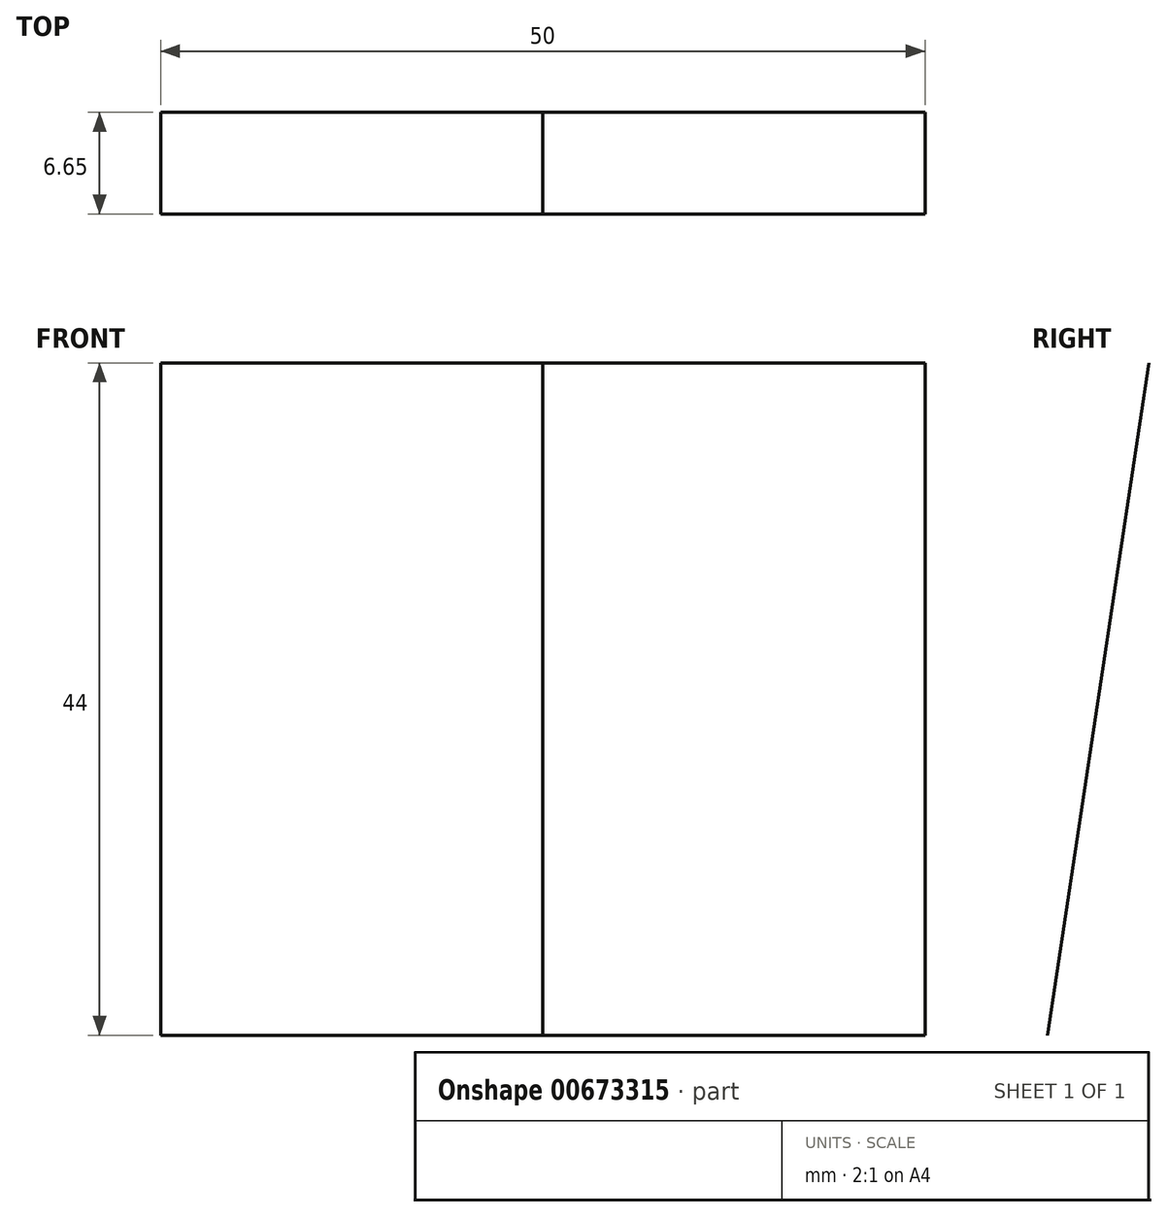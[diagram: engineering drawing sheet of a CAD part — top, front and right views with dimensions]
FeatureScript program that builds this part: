
annotation { "Feature Type Name" : "Feature", "Feature Type Description" : "" }
export const myFeature = defineFeature(function(context is Context, id is Id, definition is map)
    precondition{}
    {
        {
            var Q0;
            Q0=qCreatedBy(makeId("Right.planeOp"),FACE);
            var sketch = newSketch(context, id + "F0", { "sketchPlane" : qUnion([Q0])});
            skLineSegment(sketch, "E0", {"start": v(33.53, 0) * mm, "end": v(27.42, 43.92) * mm});
            skLineSegment(sketch, "E1", {"start": v(14.85, 44) * mm, "end": v(8.2, 0) * mm});
            skLineSegment(sketch, "E2", {"start": v(8.2, 0) * mm, "end": v(-28.06, 0) * mm});
            skPoint(sketch, "E3.visualSharp", {"position": v(21.39, 87.27) * mm});
            skArc(sketch, "E3.filletArc", {"start": v(27.42, 43.92) * mm, "mid": v(21.17, 49.4) * mm, "end": v(14.85, 44) * mm});
            skSolve(sketch);
        }
        {
            var Q0;
            Q0=sQuery(id+"F0.wireOp",EDGE,"E1");
            extrude(context, id + "F1", {"bodyType" : ToolBodyType.SURFACE, "surfaceEntities" : qUnion([Q0]), "depth" : 25 * mm, "offsetDistance" : 25 * mm});
        }
        {
            var Q0;
            Q0=makeQuery(id+"F1.opExtrude","SWEPT_BODY",BODY,{"disambiguationData":[OSD([sQuery(id+"F0.wireOp",EDGE,"E1")])]});
            var Q1;
            Q1=qCreatedBy(makeId("Right.planeOp"),FACE);
            mirror(context, id + "F2", {"entities" : qUnion([Q0]), "mirrorPlane" : qUnion([Q1])});
        }
    });
